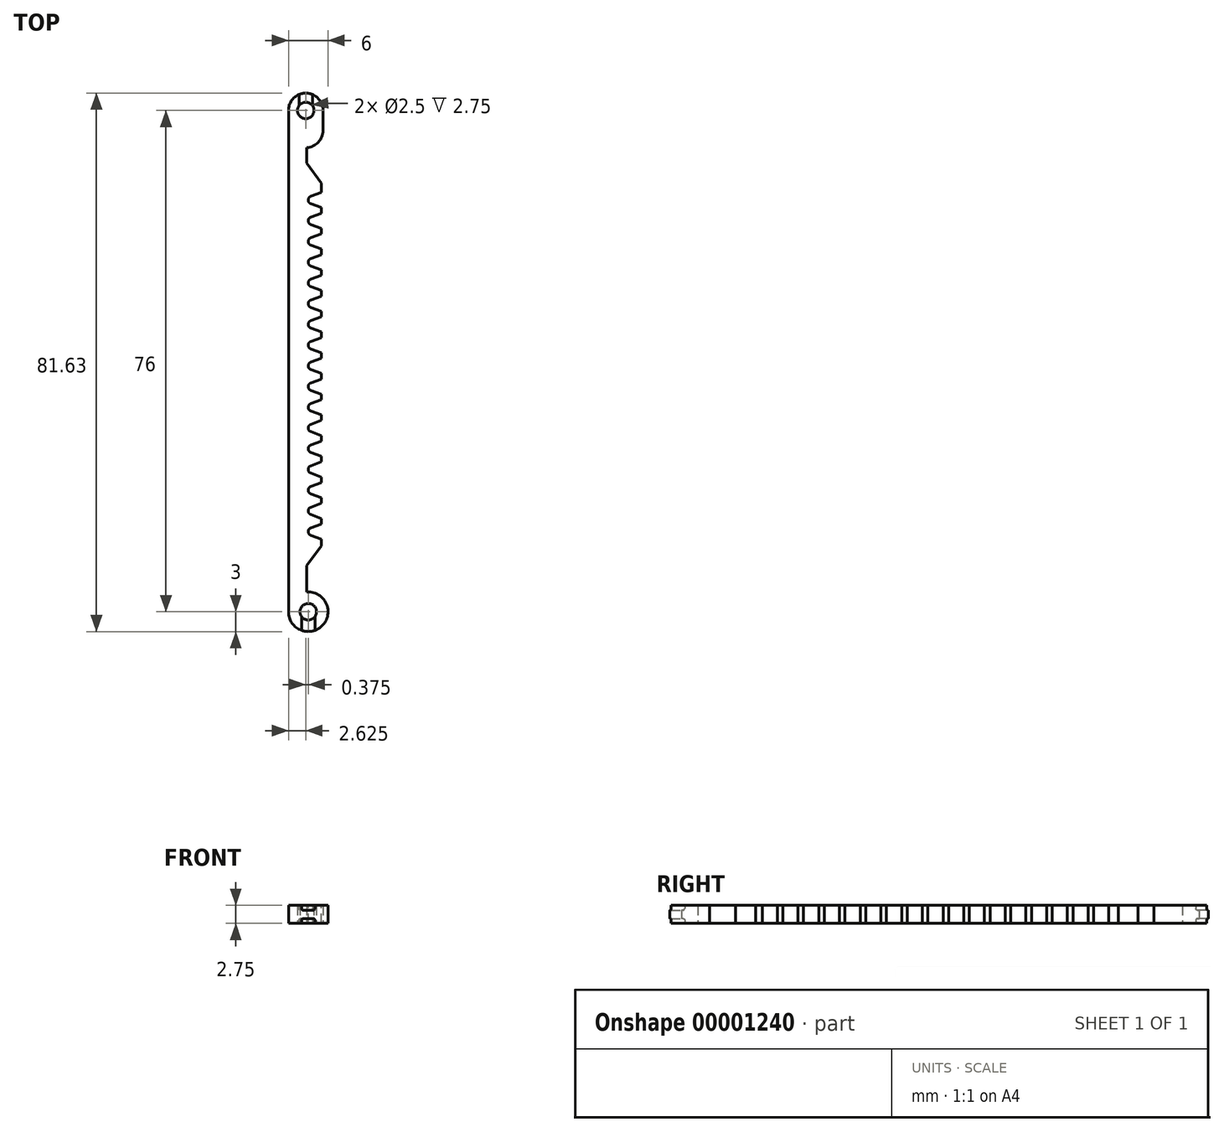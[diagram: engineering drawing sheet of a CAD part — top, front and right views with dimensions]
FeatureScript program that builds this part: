
annotation { "Feature Type Name" : "Feature", "Feature Type Description" : "" }
export const myFeature = defineFeature(function(context is Context, id is Id, definition is map)
    precondition{}
    {
        {
            var Q0;
            Q0=qCreatedBy(makeId("Top.planeOp"),FACE);
            var sketch = newSketch(context, id + "F0", { "sketchPlane" : qUnion([Q0])});
            skLineSegment(sketch, "E0.bottom", {"start": v(0, 0) * mm, "end": v(5, 0) * mm});
            skLineSegment(sketch, "E0.top", {"start": v(0, 55) * mm, "end": v(5, 55) * mm});
            skLineSegment(sketch, "E0.left", {"start": v(0, 0) * mm, "end": v(0, 55) * mm});
            skLineSegment(sketch, "E0.right", {"start": v(5, 0) * mm, "end": v(5, 55) * mm});
            skSolve(sketch);
        }
        {
            var Q0;
            Q0=makeQuery(id+"F0.imprint","IMPRINT",FACE,{"disambiguationData":[TD([[makeQuery(id+"F0.imprint","IMPRINT",EDGE,{"derivedFrom":sQuery(id+"F0.wireOp",EDGE,"E0.bottom")}),1.0]])]});
            extrude(context, id + "F1", {"entities" : qUnion([Q0]), "depth" : 2.75 * mm});
        }
        {
            var Q0;
            Q0=makeQuery(id+"F1.opExtrude","CAP_FACE",FACE,{"disambiguationData":[OSD([sQuery(id+"F0.wireOp",EDGE,"E0.bottom"),sQuery(id+"F0.wireOp",EDGE,"E0.top"),sQuery(id+"F0.wireOp",EDGE,"E0.left"),sQuery(id+"F0.wireOp",EDGE,"E0.right")])],"isStart":false});
            var sketch = newSketch(context, id + "F2", { "sketchPlane" : qUnion([Q0])});
            skLineSegment(sketch, "E1", {"start": v(5, 0) * mm, "end": v(5, 1) * mm, "construction": true});
            skLineSegment(sketch, "E2", {"start": v(5, 1) * mm, "end": v(3.4, 1.58) * mm});
            skLineSegment(sketch, "E3", {"start": v(5, 3.3) * mm, "end": v(5, 3.86) * mm, "construction": true});
            skLineSegment(sketch, "E4", {"start": v(5, 3.3) * mm, "end": v(3.4, 2.71) * mm});
            skLineSegment(sketch, "E5", {"start": v(5, 3.3) * mm, "end": v(5, 1) * mm});
            skLineSegment(sketch, "E6", {"start": v(5, 2.15) * mm, "end": v(3.6, 2.15) * mm, "construction": true});
            skPoint(sketch, "E6.endSnap0", {"position": v(5, 2.15) * mm});
            skArc(sketch, "E7", {"start": v(3.4, 2.71) * mm, "mid": v(3, 2.15) * mm, "end": v(3.4, 1.58) * mm});
            skLineSegment(sketch, "E8", {"start": v(4, 2.15) * mm, "end": v(4, 2.93) * mm, "construction": true});
            skLineSegment(sketch, "E9.1.0.0", {"start": v(5, 6.44) * mm, "end": v(3.4, 5.86) * mm});
            skArc(sketch, "E9.1.0.1", {"start": v(3.4, 5.86) * mm, "mid": v(3, 5.3) * mm, "end": v(3.4, 4.73) * mm});
            skLineSegment(sketch, "E9.1.0.2", {"start": v(5, 4.14) * mm, "end": v(3.4, 4.73) * mm});
            skLineSegment(sketch, "E9.1.0.3", {"start": v(5, 6.44) * mm, "end": v(5, 4.14) * mm});
            skLineSegment(sketch, "E9.2.0.0", {"start": v(5, 9.58) * mm, "end": v(3.4, 9) * mm});
            skArc(sketch, "E9.2.0.1", {"start": v(3.4, 9) * mm, "mid": v(3, 8.43) * mm, "end": v(3.4, 7.87) * mm});
            skLineSegment(sketch, "E9.2.0.2", {"start": v(5, 7.28) * mm, "end": v(3.4, 7.87) * mm});
            skLineSegment(sketch, "E9.2.0.3", {"start": v(5, 9.58) * mm, "end": v(5, 7.28) * mm});
            skLineSegment(sketch, "E9.direction1", {"start": v(3.4, 2.71) * mm, "end": v(3.4, 5.86) * mm, "construction": true});
            skLineSegment(sketch, "E10.0.3.0", {"start": v(5, 12.72) * mm, "end": v(3.4, 12.14) * mm});
            skArc(sketch, "E10.3.3.0", {"start": v(3.4, 12.14) * mm, "mid": v(3, 11.57) * mm, "end": v(3.4, 11) * mm});
            skLineSegment(sketch, "E10.7.3.0", {"start": v(5, 10.42) * mm, "end": v(3.4, 11) * mm});
            skLineSegment(sketch, "E10.10.3.0", {"start": v(5, 12.72) * mm, "end": v(5, 10.42) * mm});
            skLineSegment(sketch, "E10.0.4.0", {"start": v(5, 15.86) * mm, "end": v(3.4, 15.28) * mm});
            skArc(sketch, "E10.3.4.0", {"start": v(3.4, 15.28) * mm, "mid": v(3, 14.72) * mm, "end": v(3.4, 14.15) * mm});
            skLineSegment(sketch, "E10.7.4.0", {"start": v(5, 13.57) * mm, "end": v(3.4, 14.15) * mm});
            skLineSegment(sketch, "E10.10.4.0", {"start": v(5, 15.86) * mm, "end": v(5, 13.57) * mm});
            skLineSegment(sketch, "E10.0.5.0", {"start": v(5, 19) * mm, "end": v(3.4, 18.42) * mm});
            skArc(sketch, "E10.3.5.0", {"start": v(3.4, 18.42) * mm, "mid": v(3, 17.86) * mm, "end": v(3.4, 17.3) * mm});
            skLineSegment(sketch, "E10.7.5.0", {"start": v(5, 16.7) * mm, "end": v(3.4, 17.3) * mm});
            skLineSegment(sketch, "E10.10.5.0", {"start": v(5, 19) * mm, "end": v(5, 16.7) * mm});
            skLineSegment(sketch, "E10.0.6.0", {"start": v(5, 22.15) * mm, "end": v(3.4, 21.56) * mm});
            skArc(sketch, "E10.3.6.0", {"start": v(3.4, 21.56) * mm, "mid": v(3, 21) * mm, "end": v(3.4, 20.43) * mm});
            skLineSegment(sketch, "E10.7.6.0", {"start": v(5, 19.85) * mm, "end": v(3.4, 20.43) * mm});
            skLineSegment(sketch, "E10.10.6.0", {"start": v(5, 22.15) * mm, "end": v(5, 19.85) * mm});
            skLineSegment(sketch, "E10.0.7.0", {"start": v(5, 25.29) * mm, "end": v(3.4, 24.7) * mm});
            skArc(sketch, "E10.3.7.0", {"start": v(3.4, 24.7) * mm, "mid": v(3, 24.14) * mm, "end": v(3.4, 23.58) * mm});
            skLineSegment(sketch, "E10.7.7.0", {"start": v(5, 23) * mm, "end": v(3.4, 23.58) * mm});
            skLineSegment(sketch, "E10.10.7.0", {"start": v(5, 25.29) * mm, "end": v(5, 23) * mm});
            skLineSegment(sketch, "E10.0.8.0", {"start": v(5, 28.43) * mm, "end": v(3.4, 27.85) * mm});
            skArc(sketch, "E10.3.8.0", {"start": v(3.4, 27.85) * mm, "mid": v(3, 27.28) * mm, "end": v(3.4, 26.72) * mm});
            skLineSegment(sketch, "E10.7.8.0", {"start": v(5, 26.13) * mm, "end": v(3.4, 26.72) * mm});
            skLineSegment(sketch, "E10.10.8.0", {"start": v(5, 28.43) * mm, "end": v(5, 26.13) * mm});
            skLineSegment(sketch, "E10.0.9.0", {"start": v(5, 31.57) * mm, "end": v(3.4, 30.99) * mm});
            skArc(sketch, "E10.3.9.0", {"start": v(3.4, 30.99) * mm, "mid": v(3, 30.42) * mm, "end": v(3.4, 29.86) * mm});
            skLineSegment(sketch, "E10.7.9.0", {"start": v(5, 29.27) * mm, "end": v(3.4, 29.86) * mm});
            skLineSegment(sketch, "E10.10.9.0", {"start": v(5, 31.57) * mm, "end": v(5, 29.27) * mm});
            skLineSegment(sketch, "E11.0.10.0", {"start": v(5, 34.71) * mm, "end": v(3.4, 34.13) * mm});
            skArc(sketch, "E11.3.10.0", {"start": v(3.4, 34.13) * mm, "mid": v(3, 33.56) * mm, "end": v(3.4, 33) * mm});
            skLineSegment(sketch, "E11.7.10.0", {"start": v(5, 32.42) * mm, "end": v(3.4, 33) * mm});
            skLineSegment(sketch, "E11.10.10.0", {"start": v(5, 34.71) * mm, "end": v(5, 32.42) * mm});
            skLineSegment(sketch, "E11.0.11.0", {"start": v(5, 37.86) * mm, "end": v(3.4, 37.27) * mm});
            skArc(sketch, "E11.3.11.0", {"start": v(3.4, 37.27) * mm, "mid": v(3, 36.7) * mm, "end": v(3.4, 36.14) * mm});
            skLineSegment(sketch, "E11.7.11.0", {"start": v(5, 35.56) * mm, "end": v(3.4, 36.14) * mm});
            skLineSegment(sketch, "E11.10.11.0", {"start": v(5, 37.86) * mm, "end": v(5, 35.56) * mm});
            skLineSegment(sketch, "E11.0.12.0", {"start": v(5, 41) * mm, "end": v(3.4, 40.41) * mm});
            skArc(sketch, "E11.3.12.0", {"start": v(3.4, 40.41) * mm, "mid": v(3, 39.85) * mm, "end": v(3.4, 39.28) * mm});
            skLineSegment(sketch, "E11.7.12.0", {"start": v(5, 38.7) * mm, "end": v(3.4, 39.28) * mm});
            skLineSegment(sketch, "E11.10.12.0", {"start": v(5, 41) * mm, "end": v(5, 38.7) * mm});
            skLineSegment(sketch, "E11.0.13.0", {"start": v(5, 44.14) * mm, "end": v(3.4, 43.55) * mm});
            skArc(sketch, "E11.3.13.0", {"start": v(3.4, 43.55) * mm, "mid": v(3, 42.99) * mm, "end": v(3.4, 42.42) * mm});
            skLineSegment(sketch, "E11.7.13.0", {"start": v(5, 41.84) * mm, "end": v(3.4, 42.42) * mm});
            skLineSegment(sketch, "E11.10.13.0", {"start": v(5, 44.14) * mm, "end": v(5, 41.84) * mm});
            skLineSegment(sketch, "E11.0.14.0", {"start": v(5, 47.28) * mm, "end": v(3.4, 46.7) * mm});
            skArc(sketch, "E11.3.14.0", {"start": v(3.4, 46.7) * mm, "mid": v(3, 46.13) * mm, "end": v(3.4, 45.57) * mm});
            skLineSegment(sketch, "E11.7.14.0", {"start": v(5, 44.98) * mm, "end": v(3.4, 45.57) * mm});
            skLineSegment(sketch, "E11.10.14.0", {"start": v(5, 47.28) * mm, "end": v(5, 44.98) * mm});
            skLineSegment(sketch, "E12.0.15.0", {"start": v(5, 50.42) * mm, "end": v(3.4, 49.84) * mm});
            skArc(sketch, "E12.3.15.0", {"start": v(3.4, 49.84) * mm, "mid": v(3, 49.27) * mm, "end": v(3.4, 48.7) * mm});
            skLineSegment(sketch, "E12.7.15.0", {"start": v(5, 48.12) * mm, "end": v(3.4, 48.7) * mm});
            skLineSegment(sketch, "E12.10.15.0", {"start": v(5, 50.42) * mm, "end": v(5, 48.12) * mm});
            skLineSegment(sketch, "E13.0.16.0", {"start": v(5, 53.56) * mm, "end": v(3.4, 52.98) * mm});
            skArc(sketch, "E13.3.16.0", {"start": v(3.4, 52.98) * mm, "mid": v(3, 52.41) * mm, "end": v(3.4, 51.85) * mm});
            skLineSegment(sketch, "E13.7.16.0", {"start": v(5, 51.27) * mm, "end": v(3.4, 51.85) * mm});
            skLineSegment(sketch, "E13.10.16.0", {"start": v(5, 53.56) * mm, "end": v(5, 51.27) * mm});
            skSolve(sketch);
        }
        {
            var Q0;
            Q0 = qSketchRegion(id + "F2", true);
            extrude(context, id + "F3", {"entities" : qUnion([Q0]), "operationType" : NewBodyOperationType.REMOVE, "endBound" : BoundingType.UP_TO_NEXT, "oppositeDirection" : true, "depth" : 25 * mm});
        }
        {
            var Q0;
            Q0=qCreatedBy(makeId("Top.planeOp"),FACE);
            var sketch = newSketch(context, id + "F4", { "sketchPlane" : qUnion([Q0])});
            skLineSegment(sketch, "E14", {"start": v(0, 63) * mm, "end": v(0, 55) * mm});
            skLineSegment(sketch, "E15", {"start": v(0, 55) * mm, "end": v(5, 55) * mm});
            skLineSegment(sketch, "E16", {"start": v(5, 55) * mm, "end": v(2.75, 58) * mm});
            skLineSegment(sketch, "E17", {"start": v(2.75, 58) * mm, "end": v(2.75, 60.38) * mm});
            skArc(sketch, "E18", {"start": v(2.75, 60.38) * mm, "mid": v(4.52, 61.19) * mm, "end": v(5.25, 63) * mm});
            skLineSegment(sketch, "E19", {"start": v(0, 0) * mm, "end": v(0, -10) * mm});
            skCircle(sketch, "E20", {"center": v(3, -10) * mm, "radius": 1.25 * mm});
            skArc(sketch, "E21", {"start": v(0, -10) * mm, "mid": v(5.2, -12.03) * mm, "end": v(2.75, -7.01) * mm});
            skLineSegment(sketch, "E22", {"start": v(0, 0) * mm, "end": v(5, 0) * mm});
            skLineSegment(sketch, "E23", {"start": v(5, 0) * mm, "end": v(2.75, -3) * mm});
            skLineSegment(sketch, "E24", {"start": v(2.75, -3) * mm, "end": v(2.75, -7.01) * mm});
            skLineSegment(sketch, "E25", {"start": v(0, 63) * mm, "end": v(0, 66) * mm});
            skLineSegment(sketch, "E26", {"start": v(5.25, 63) * mm, "end": v(5.25, 66) * mm});
            skArc(sketch, "E27", {"start": v(5.25, 66) * mm, "mid": v(2.62, 68.62) * mm, "end": v(0, 66) * mm});
            skCircle(sketch, "E28", {"center": v(2.62, 66) * mm, "radius": 1.25 * mm});
            skSolve(sketch);
        }
        {
            var Q0;
            Q0=makeQuery(id+"F4.imprint","IMPRINT",FACE,{"disambiguationData":[TD([[makeQuery(id+"F4.imprint","IMPRINT",EDGE,{"derivedFrom":sQuery(id+"F4.wireOp",EDGE,"E14")}),1.0]])]});
            var Q1;
            Q1=makeQuery(id+"F4.imprint","IMPRINT",FACE,{"disambiguationData":[TD([[makeQuery(id+"F4.imprint","IMPRINT",EDGE,{"derivedFrom":sQuery(id+"F4.wireOp",EDGE,"E19")}),1.0]])]});
            var Q2;
            Q2=makeQuery(id+"F1.opExtrude","CAP_FACE",FACE,{"disambiguationData":[OSD([sQuery(id+"F0.wireOp",EDGE,"E0.bottom"),sQuery(id+"F0.wireOp",EDGE,"E0.top"),sQuery(id+"F0.wireOp",EDGE,"E0.left"),sQuery(id+"F0.wireOp",EDGE,"E0.right")])],"isStart":false});
            extrude(context, id + "F5", {"entities" : qUnion([Q0, Q1]), "operationType" : NewBodyOperationType.ADD, "endBound" : BoundingType.UP_TO_SURFACE, "endBoundEntityFace" : qUnion([Q2]), "depth" : 25 * mm});
        }
        {
            var Q0;
            Q0=makeQuery(id+"F5.boolean.opBoolean","MERGE",FACE,{"derivedFrom":[makeQuery(id+"F1.opExtrude","CAP_FACE",FACE,{"disambiguationData":[OSD([sQuery(id+"F0.wireOp",EDGE,"E0.bottom"),sQuery(id+"F0.wireOp",EDGE,"E0.top"),sQuery(id+"F0.wireOp",EDGE,"E0.left"),sQuery(id+"F0.wireOp",EDGE,"E0.right")])],"isStart":true}),makeQuery(id+"F5.opExtrude","CAP_FACE",FACE,{"disambiguationData":[OSD([sQuery(id+"F4.wireOp",EDGE,"E14"),sQuery(id+"F4.wireOp",EDGE,"E15"),sQuery(id+"F4.wireOp",EDGE,"E16"),sQuery(id+"F4.wireOp",EDGE,"E17"),sQuery(id+"F4.wireOp",EDGE,"E18"),sQuery(id+"F4.wireOp",EDGE,"b6379942-12da-4af8-a4e3-6cbcfb0f5488")])],"isStart":true}),makeQuery(id+"F5.opExtrude","CAP_FACE",FACE,{"disambiguationData":[OSD([sQuery(id+"F4.wireOp",EDGE,"E19"),sQuery(id+"F4.wireOp",EDGE,"E20"),sQuery(id+"F4.wireOp",EDGE,"E21"),sQuery(id+"F4.wireOp",EDGE,"E22"),sQuery(id+"F4.wireOp",EDGE,"E23"),sQuery(id+"F4.wireOp",EDGE,"E24")])],"isStart":true})]});
            var sketch = newSketch(context, id + "F6", { "sketchPlane" : qUnion([Q0])});
            skArc(sketch, "E29", {"start": v(1.35, -59) * mm, "mid": v(2.05, -59.7) * mm, "end": v(2.75, -59) * mm});
            skArc(sketch, "E30", {"start": v(2.75, -55.5) * mm, "mid": v(2.05, -54.8) * mm, "end": v(1.35, -55.5) * mm});
            skLineSegment(sketch, "E31", {"start": v(2.05, -59) * mm, "end": v(2.05, -55.5) * mm, "construction": true});
            skLineSegment(sketch, "E32", {"start": v(1.35, -59) * mm, "end": v(1.35, -55.5) * mm});
            skLineSegment(sketch, "E33", {"start": v(2.75, -59) * mm, "end": v(2.75, -55.5) * mm});
            skPoint(sketch, "E34", {"position": v(2.62, -63) * mm});
            skSolve(sketch);
        }
        {
            var Q0;
            Q0=makeQuery(id+"F5.opExtrude","SWEPT_EDGE",EDGE,{"disambiguationData":[OSD([sQuery(id+"F4.wireOp",EDGE,"E19"),sQuery(id+"F4.wireOp",EDGE,"E21")])]});
            cPlane(context, id + "F7", {"entities" : qUnion([Q0]), "cplaneType" : CPlaneType.LINE_ANGLE, "offset" : 150 * mm, "angle" : 90 * degree, "width" : 150 * mm, "height" : 150 * mm});
        }
        {
            var Q0;
            Q0=qCreatedBy(id+"F7.planeOp",FACE);
            var sketch = newSketch(context, id + "F8", { "sketchPlane" : qUnion([Q0])});
            skLineSegment(sketch, "E35.bottom", {"start": v(-2, 3.5) * mm, "end": v(-4, 3.5) * mm});
            skLineSegment(sketch, "E35.top", {"start": v(-2, 2) * mm, "end": v(-4, 2) * mm});
            skLineSegment(sketch, "E35.left", {"start": v(-2, 3.5) * mm, "end": v(-2, 2) * mm});
            skLineSegment(sketch, "E35.right", {"start": v(-4, 3.5) * mm, "end": v(-4, 2) * mm});
            skPoint(sketch, "E35.middle", {"position": v(-3, 2.75) * mm});
            skLineSegment(sketch, "E36.bottom", {"start": v(-4, 0.75) * mm, "end": v(-2, 0.75) * mm});
            skLineSegment(sketch, "E36.top", {"start": v(-4, -0.75) * mm, "end": v(-2, -0.75) * mm});
            skLineSegment(sketch, "E36.left", {"start": v(-4, 0.75) * mm, "end": v(-4, -0.75) * mm});
            skLineSegment(sketch, "E36.right", {"start": v(-2, 0.75) * mm, "end": v(-2, -0.75) * mm});
            skPoint(sketch, "E36.middle", {"position": v(-3, 0) * mm});
            skSolve(sketch);
        }
        {
            var Q0;
            Q0=makeQuery(id+"F8.imprint","IMPRINT",FACE,{"disambiguationData":[TD([[makeQuery(id+"F8.imprint","IMPRINT",EDGE,{"derivedFrom":sQuery(id+"F8.wireOp",EDGE,"E35.bottom")}),1.0]])]});
            var Q1;
            Q1=makeQuery(id+"F8.imprint","IMPRINT",FACE,{"disambiguationData":[TD([[makeQuery(id+"F8.imprint","IMPRINT",EDGE,{"derivedFrom":sQuery(id+"F8.wireOp",EDGE,"E36.bottom")}),-1.0]])]});
            extrude(context, id + "F9", {"entities" : qUnion([Q0, Q1]), "operationType" : NewBodyOperationType.REMOVE, "endBound" : BoundingType.THROUGH_ALL, "oppositeDirection" : true, "depth" : 25 * mm});
        }
        {
            var Q0;
            Q0=qCreatedBy(id+"F7.planeOp",FACE);
            var Q1;
            Q1=sQuery(id+"F4.wireOp",VERTEX,"E27.center");
            cPlane(context, id + "F10", {"entities" : qUnion([Q0, Q1]), "cplaneType" : CPlaneType.PLANE_POINT, "offset" : 150 * mm, "width" : 150 * mm, "height" : 150 * mm});
        }
        {
            var Q0;
            Q0=qCreatedBy(id+"F10.planeOp",FACE);
            var sketch = newSketch(context, id + "F11", { "sketchPlane" : qUnion([Q0])});
            skLineSegment(sketch, "E37.bottom", {"start": v(-3.63, -0.75) * mm, "end": v(-1.63, -0.75) * mm});
            skLineSegment(sketch, "E37.top", {"start": v(-3.63, 0.75) * mm, "end": v(-1.63, 0.75) * mm});
            skLineSegment(sketch, "E37.left", {"start": v(-3.63, -0.75) * mm, "end": v(-3.63, 0.75) * mm});
            skLineSegment(sketch, "E37.right", {"start": v(-1.63, -0.75) * mm, "end": v(-1.63, 0.75) * mm});
            skPoint(sketch, "E37.middle", {"position": v(-2.63, 0) * mm});
            skLineSegment(sketch, "E38.bottom", {"start": v(-3.63, 3.5) * mm, "end": v(-1.63, 3.5) * mm});
            skLineSegment(sketch, "E38.top", {"start": v(-3.63, 2) * mm, "end": v(-1.63, 2) * mm});
            skLineSegment(sketch, "E38.left", {"start": v(-3.63, 3.5) * mm, "end": v(-3.63, 2) * mm});
            skLineSegment(sketch, "E38.right", {"start": v(-1.63, 3.5) * mm, "end": v(-1.63, 2) * mm});
            skPoint(sketch, "E38.middle", {"position": v(-2.63, 2.75) * mm});
            skLineSegment(sketch, "E39.0", {"start": v(-3.88, 0) * mm, "end": v(-1.38, 0) * mm});
            skLineSegment(sketch, "E40.0", {"start": v(-3.88, 2.75) * mm, "end": v(-1.38, 2.75) * mm});
            skSolve(sketch);
        }
        {
            var Q0;
            {var subQ0=sQuery(id+"F11.wireOp",EDGE,"E37.top");Q0=makeQuery(id+"F11.imprint","IMPRINT",FACE,{"disambiguationData":[TD([[makeQuery(id+"F11.imprint","IMPRINT",EDGE,{"derivedFrom":subQ0}),-1.0]])]});}
            var Q1;
            {var subQ0=sQuery(id+"F11.wireOp",EDGE,"E38.top");Q1=makeQuery(id+"F11.imprint","IMPRINT",FACE,{"disambiguationData":[TD([[makeQuery(id+"F11.imprint","IMPRINT",EDGE,{"derivedFrom":subQ0}),1.0]])]});}
            extrude(context, id + "F12", {"entities" : qUnion([Q0, Q1]), "operationType" : NewBodyOperationType.REMOVE, "endBound" : BoundingType.THROUGH_ALL, "depth" : 25 * mm});
        }
        {
            var Q0;
            Q0=makeQuery(id+"F9.boolean.opBoolean","COPY",EDGE,{"derivedFrom":makeQuery(id+"F9.opExtrude","SWEPT_EDGE",EDGE,{"disambiguationData":[OSD([sQuery(id+"F8.wireOp",EDGE,"E35.top"),sQuery(id+"F8.wireOp",EDGE,"E35.left")])]})});
            var Q1;
            Q1=makeQuery(id+"F9.boolean.opBoolean","COPY",EDGE,{"derivedFrom":makeQuery(id+"F9.opExtrude","SWEPT_EDGE",EDGE,{"disambiguationData":[OSD([sQuery(id+"F8.wireOp",EDGE,"E35.top"),sQuery(id+"F8.wireOp",EDGE,"E35.right")])]})});
            var Q2;
            Q2=makeQuery(id+"F9.boolean.opBoolean","COPY",EDGE,{"derivedFrom":makeQuery(id+"F9.opExtrude","SWEPT_EDGE",EDGE,{"disambiguationData":[OSD([sQuery(id+"F8.wireOp",EDGE,"E36.bottom"),sQuery(id+"F8.wireOp",EDGE,"E36.right")])]})});
            var Q3;
            Q3=makeQuery(id+"F9.boolean.opBoolean","COPY",EDGE,{"derivedFrom":makeQuery(id+"F9.opExtrude","SWEPT_EDGE",EDGE,{"disambiguationData":[OSD([sQuery(id+"F8.wireOp",EDGE,"E36.bottom"),sQuery(id+"F8.wireOp",EDGE,"E36.left")])]})});
            var Q4;
            Q4=makeQuery(id+"F12.boolean.opBoolean","COPY",EDGE,{"derivedFrom":makeQuery(id+"F12.opExtrude","SWEPT_EDGE",EDGE,{"disambiguationData":[OSD([sQuery(id+"F11.wireOp",EDGE,"E37.top"),sQuery(id+"F11.wireOp",EDGE,"E37.right")])]})});
            var Q5;
            Q5=makeQuery(id+"F12.boolean.opBoolean","COPY",EDGE,{"derivedFrom":makeQuery(id+"F12.opExtrude","SWEPT_EDGE",EDGE,{"disambiguationData":[OSD([sQuery(id+"F11.wireOp",EDGE,"E38.top"),sQuery(id+"F11.wireOp",EDGE,"E38.right")])]})});
            var Q6;
            Q6=makeQuery(id+"F12.boolean.opBoolean","COPY",EDGE,{"derivedFrom":makeQuery(id+"F12.opExtrude","SWEPT_EDGE",EDGE,{"disambiguationData":[OSD([sQuery(id+"F11.wireOp",EDGE,"E38.top"),sQuery(id+"F11.wireOp",EDGE,"E38.left")])]})});
            var Q7;
            Q7=makeQuery(id+"F12.boolean.opBoolean","COPY",EDGE,{"derivedFrom":makeQuery(id+"F12.opExtrude","SWEPT_EDGE",EDGE,{"disambiguationData":[OSD([sQuery(id+"F11.wireOp",EDGE,"E37.top"),sQuery(id+"F11.wireOp",EDGE,"E37.left")])]})});
            fillet(context, id + "F13", {"entities" : qUnion([Q0, Q1, Q2, Q3, Q4, Q5, Q6, Q7]), "radius" : 0.25 * mm, "tangentPropagation" : true, "allowEdgeOverflow" : false});
        }
    });
